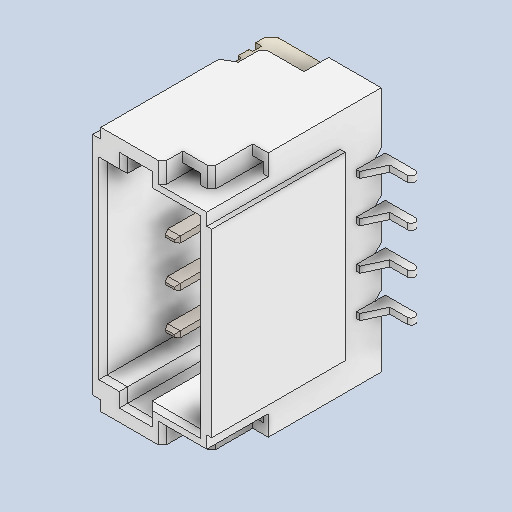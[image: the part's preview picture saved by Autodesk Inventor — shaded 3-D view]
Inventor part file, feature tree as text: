
AUTODESK INVENTOR PART (.ipt)
format: ipt  version: 2024.3 (Build 283343000, 343)  size: 277,504 bytes
history: native  units: in
note: dims shown in document units (in); Inventor stores cm internally (conversion verified against a paired STEP export)
features: other x8, mirror x2, chamfer x1
ambient origin geometry x8: Origin, YZ Plane, XZ Plane, XY Plane, X Axis, Y Axis, Z Axis, Center Point
bodies: Solid1 (feature_tree), Solid2 (feature_tree), Solid3 (feature_tree), Solid4 (feature_tree), Solid5 (feature_tree), Solid6 (feature_tree), Solid7 (feature_tree), Solid8 (feature_tree), Solid9 (feature_tree), Solid10 (feature_tree), Solid11 (feature_tree)
feature tree (11):
  other  "Boss-Extrude2"
  other  "Body-Move_Copy2"
  other  "Body-Move_Copy3"
  other  "Body-Move_Copy4"
  other  "Boss-Extrude3"
  chamfer  "Chamfer3"  [1 undecoded]
  other  "LPattern2[1]"
  other  "LPattern2[2]"
  other  "LPattern2[3]"
  mirror  "Mirror2"
  mirror  "Mirror3"
note: 1 required parameter value undecoded (feature->parameter linkage not recoverable at this tier; creation-order binding heuristic only, values carry confidence <= 0.55)
